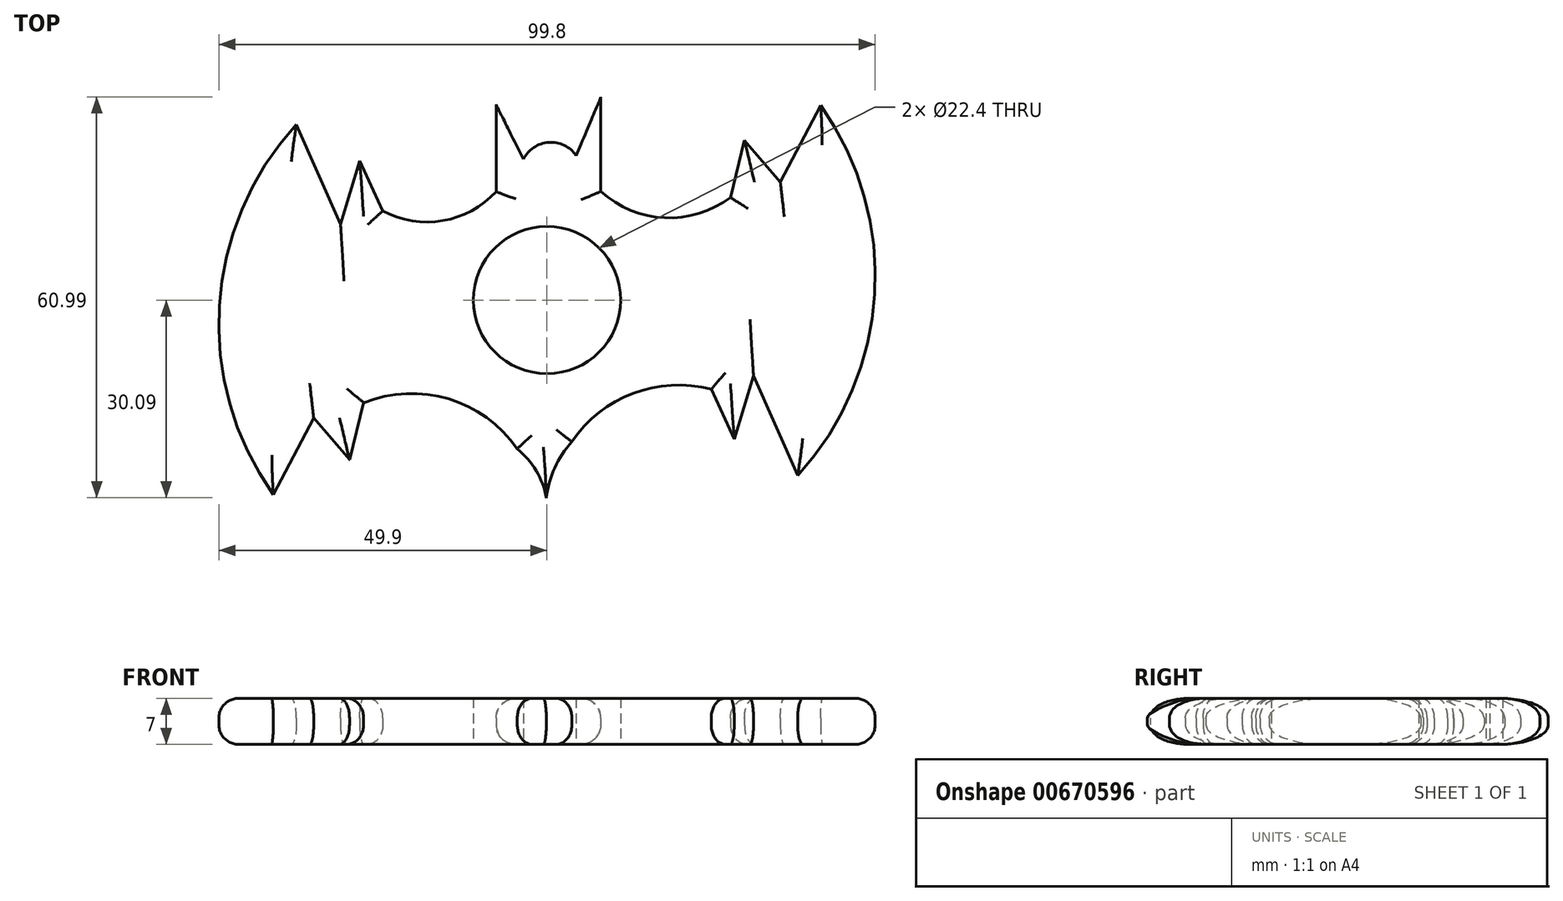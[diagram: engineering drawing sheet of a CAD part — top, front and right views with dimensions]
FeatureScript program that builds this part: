
annotation { "Feature Type Name" : "Feature", "Feature Type Description" : "" }
export const myFeature = defineFeature(function(context is Context, id is Id, definition is map)
    precondition{}
    {
        {
            var Q0;
            Q0=qCreatedBy(makeId("Top.planeOp"),FACE);
            var sketch = newSketch(context, id + "F0", { "sketchPlane" : qUnion([Q0])});
            skCircle(sketch, "E0", {"center": v(0, 0) * mm, "radius": 11.2 * mm});
            skCircle(sketch, "E1", {"center": v(0, 0) * mm, "radius": 13.2 * mm});
            skArc(sketch, "E2", {"start": v(-38.1, 26.72) * mm, "mid": v(-49.82, -0.84) * mm, "end": v(-41.61, -29.64) * mm});
            skArc(sketch, "E3.1.0", {"start": v(38.1, -26.72) * mm, "mid": v(49.82, 0.84) * mm, "end": v(41.61, 29.64) * mm});
            skLineSegment(sketch, "E4", {"start": v(-41.61, -29.64) * mm, "end": v(-35.48, -17.96) * mm});
            skLineSegment(sketch, "E5", {"start": v(-35.48, -17.96) * mm, "end": v(-35.48, -24.97) * mm});
            skArc(sketch, "E6", {"start": v(-4.53, -22.63) * mm, "mid": v(-14.98, -15.03) * mm, "end": v(-27.89, -15.62) * mm});
            skLineSegment(sketch, "E7.1.0", {"start": v(41.61, 29.64) * mm, "end": v(35.48, 17.96) * mm});
            skLineSegment(sketch, "E7.1.1", {"start": v(35.48, 17.96) * mm, "end": v(30.03, 24.29) * mm});
            skLineSegment(sketch, "E7.1.2", {"start": v(30.03, 24.29) * mm, "end": v(27.89, 15.62) * mm});
            skLineSegment(sketch, "E8", {"start": v(38.1, -26.72) * mm, "end": v(31.4, -11.53) * mm});
            skLineSegment(sketch, "E9", {"start": v(31.4, -11.53) * mm, "end": v(28.47, -21.17) * mm});
            skLineSegment(sketch, "E10", {"start": v(28.47, -21.17) * mm, "end": v(24.97, -13.58) * mm});
            skArc(sketch, "E11.1.0", {"start": v(-24.97, 13.58) * mm, "mid": v(-15.85, 12.08) * mm, "end": v(-7.74, 16.5) * mm});
            skLineSegment(sketch, "E11.1.2", {"start": v(-28.47, 21.17) * mm, "end": v(-24.97, 13.58) * mm});
            skLineSegment(sketch, "E11.1.4", {"start": v(-31.4, 11.53) * mm, "end": v(-28.47, 21.17) * mm});
            skLineSegment(sketch, "E11.1.5", {"start": v(-38.1, 26.72) * mm, "end": v(-31.4, 11.53) * mm});
            skArc(sketch, "E12", {"start": v(0, -34.06) * mm, "mid": v(-0.76, -27.75) * mm, "end": v(-4.53, -22.63) * mm});
            skArc(sketch, "E13.1.0", {"start": v(8.2, 16.53) * mm, "mid": v(17.88, 12.52) * mm, "end": v(27.89, 15.62) * mm});
            skLineSegment(sketch, "E14", {"start": v(-7.74, 16.5) * mm, "end": v(-7.74, 29.75) * mm});
            skLineSegment(sketch, "E15", {"start": v(-7.74, 29.75) * mm, "end": v(-3.6, 21.41) * mm});
            skLineSegment(sketch, "E16", {"start": v(8.2, 16.53) * mm, "end": v(8.2, 30.9) * mm});
            skLineSegment(sketch, "E17", {"start": v(8.2, 30.9) * mm, "end": v(4.45, 21.97) * mm});
            skArc(sketch, "E18", {"start": v(4.45, 21.97) * mm, "mid": v(0.27, 24) * mm, "end": v(-3.6, 21.41) * mm});
            skArc(sketch, "E19", {"start": v(24.97, -13.58) * mm, "mid": v(13.1, -14.2) * mm, "end": v(3.78, -21.57) * mm});
            skArc(sketch, "E20", {"start": v(3.78, -21.57) * mm, "mid": v(0.47, -27.38) * mm, "end": v(0, -34.06) * mm});
            skLineSegment(sketch, "E21.1.0", {"start": v(-35.48, -17.96) * mm, "end": v(-30.03, -24.29) * mm});
            skLineSegment(sketch, "E21.1.1", {"start": v(-30.03, -24.29) * mm, "end": v(-27.89, -15.62) * mm});
            skSolve(sketch);
        }
        {
            var Q0;
            Q0=makeQuery(id+"F0.imprint","IMPRINT",FACE,{"disambiguationData":[TD([[makeQuery(id+"F0.imprint","IMPRINT",EDGE,{"derivedFrom":sQuery(id+"F0.wireOp",EDGE,"E0")}),-1.0]])]});
            var Q1;
            Q1=makeQuery(id+"F0.imprint","IMPRINT",FACE,{"disambiguationData":[TD([[makeQuery(id+"F0.imprint","IMPRINT",EDGE,{"derivedFrom":sQuery(id+"F0.wireOp",EDGE,"E1")}),-1.0]])]});
            extrude(context, id + "F1", {"entities" : qUnion([Q0, Q1]), "depth" : 7 * mm, "offsetDistance" : 25 * mm});
        }
        {
            var Q0;
            Q0=makeQuery(id+"F1.opExtrude","CAP_EDGE",EDGE,{"disambiguationData":[OSD([sQuery(id+"F0.wireOp",EDGE,"E20")])],"isStart":false});
            var Q1;
            Q1=makeQuery(id+"F1.opExtrude","CAP_EDGE",EDGE,{"disambiguationData":[OSD([sQuery(id+"F0.wireOp",EDGE,"E19")])],"isStart":false});
            var Q2;
            Q2=makeQuery(id+"F1.opExtrude","CAP_EDGE",EDGE,{"disambiguationData":[OSD([sQuery(id+"F0.wireOp",EDGE,"E9")])],"isStart":false});
            var Q3;
            Q3=makeQuery(id+"F1.opExtrude","CAP_EDGE",EDGE,{"disambiguationData":[OSD([sQuery(id+"F0.wireOp",EDGE,"E3.1.0")])],"isStart":false});
            var Q4;
            Q4=makeQuery(id+"F1.opExtrude","CAP_EDGE",EDGE,{"disambiguationData":[OSD([sQuery(id+"F0.wireOp",EDGE,"E8")])],"isStart":false});
            var Q5;
            Q5=makeQuery(id+"F1.opExtrude","CAP_EDGE",EDGE,{"disambiguationData":[OSD([sQuery(id+"F0.wireOp",EDGE,"E7.1.0")])],"isStart":false});
            var Q6;
            Q6=makeQuery(id+"F1.opExtrude","CAP_EDGE",EDGE,{"disambiguationData":[OSD([sQuery(id+"F0.wireOp",EDGE,"E7.1.1")])],"isStart":false});
            var Q7;
            Q7=makeQuery(id+"F1.opExtrude","CAP_EDGE",EDGE,{"disambiguationData":[OSD([sQuery(id+"F0.wireOp",EDGE,"E7.1.2")])],"isStart":false});
            var Q8;
            Q8=makeQuery(id+"F1.opExtrude","CAP_EDGE",EDGE,{"disambiguationData":[OSD([sQuery(id+"F0.wireOp",EDGE,"E13.1.0")])],"isStart":false});
            var Q9;
            Q9=makeQuery(id+"F1.opExtrude","CAP_EDGE",EDGE,{"disambiguationData":[OSD([sQuery(id+"F0.wireOp",EDGE,"E16")])],"isStart":false});
            var Q10;
            Q10=makeQuery(id+"F1.opExtrude","CAP_EDGE",EDGE,{"disambiguationData":[OSD([sQuery(id+"F0.wireOp",EDGE,"E14")])],"isStart":false});
            var Q11;
            Q11=makeQuery(id+"F1.opExtrude","CAP_EDGE",EDGE,{"disambiguationData":[OSD([sQuery(id+"F0.wireOp",EDGE,"E11.1.0")])],"isStart":false});
            var Q12;
            Q12=makeQuery(id+"F1.opExtrude","CAP_EDGE",EDGE,{"disambiguationData":[OSD([sQuery(id+"F0.wireOp",EDGE,"E11.1.2")])],"isStart":false});
            var Q13;
            Q13=makeQuery(id+"F1.opExtrude","CAP_EDGE",EDGE,{"disambiguationData":[OSD([sQuery(id+"F0.wireOp",EDGE,"E11.1.5")])],"isStart":false});
            var Q14;
            Q14=makeQuery(id+"F1.opExtrude","CAP_EDGE",EDGE,{"disambiguationData":[OSD([sQuery(id+"F0.wireOp",EDGE,"E11.1.4")])],"isStart":false});
            var Q15;
            Q15=makeQuery(id+"F1.opExtrude","CAP_EDGE",EDGE,{"disambiguationData":[OSD([sQuery(id+"F0.wireOp",EDGE,"E2")])],"isStart":false});
            var Q16;
            Q16=makeQuery(id+"F1.opExtrude","CAP_EDGE",EDGE,{"disambiguationData":[OSD([sQuery(id+"F0.wireOp",EDGE,"E4")])],"isStart":false});
            var Q17;
            Q17=makeQuery(id+"F1.opExtrude","CAP_EDGE",EDGE,{"disambiguationData":[OSD([sQuery(id+"F0.wireOp",EDGE,"wEF84jsq-XExs-cQrN-D3yr-Ib7uIkRzdJAm")])],"isStart":false});
            var Q18;
            Q18=makeQuery(id+"F1.opExtrude","CAP_EDGE",EDGE,{"disambiguationData":[OSD([sQuery(id+"F0.wireOp",EDGE,"E12")])],"isStart":false});
            var Q19;
            Q19=makeQuery(id+"F1.opExtrude","CAP_EDGE",EDGE,{"disambiguationData":[OSD([sQuery(id+"F0.wireOp",EDGE,"E5")])],"isStart":false});
            var Q20;
            Q20=makeQuery(id+"F1.opExtrude","CAP_EDGE",EDGE,{"disambiguationData":[OSD([sQuery(id+"F0.wireOp",EDGE,"E10")])],"isStart":false});
            var Q21;
            Q21=makeQuery(id+"F1.opExtrude","CAP_EDGE",EDGE,{"disambiguationData":[OSD([sQuery(id+"F0.wireOp",EDGE,"E21.1.1")])],"isStart":false});
            var Q22;
            Q22=makeQuery(id+"F1.opExtrude","CAP_EDGE",EDGE,{"disambiguationData":[OSD([sQuery(id+"F0.wireOp",EDGE,"E6")])],"isStart":false});
            var Q23;
            Q23=makeQuery(id+"F1.opExtrude","CAP_EDGE",EDGE,{"disambiguationData":[OSD([sQuery(id+"F0.wireOp",EDGE,"E21.1.0")])],"isStart":false});
            var Q24;
            Q24=makeQuery(id+"F1.opExtrude","CAP_EDGE",EDGE,{"disambiguationData":[OSD([sQuery(id+"F0.wireOp",EDGE,"E3.1.0")])],"isStart":true});
            var Q25;
            Q25=makeQuery(id+"F1.opExtrude","CAP_EDGE",EDGE,{"disambiguationData":[OSD([sQuery(id+"F0.wireOp",EDGE,"E8")])],"isStart":true});
            var Q26;
            Q26=makeQuery(id+"F1.opExtrude","CAP_EDGE",EDGE,{"disambiguationData":[OSD([sQuery(id+"F0.wireOp",EDGE,"E9")])],"isStart":true});
            var Q27;
            Q27=makeQuery(id+"F1.opExtrude","CAP_EDGE",EDGE,{"disambiguationData":[OSD([sQuery(id+"F0.wireOp",EDGE,"E10")])],"isStart":true});
            var Q28;
            Q28=makeQuery(id+"F1.opExtrude","CAP_EDGE",EDGE,{"disambiguationData":[OSD([sQuery(id+"F0.wireOp",EDGE,"E19")])],"isStart":true});
            var Q29;
            Q29=makeQuery(id+"F1.opExtrude","CAP_EDGE",EDGE,{"disambiguationData":[OSD([sQuery(id+"F0.wireOp",EDGE,"E6")])],"isStart":true});
            var Q30;
            Q30=makeQuery(id+"F1.opExtrude","CAP_EDGE",EDGE,{"disambiguationData":[OSD([sQuery(id+"F0.wireOp",EDGE,"E12")])],"isStart":true});
            var Q31;
            Q31=makeQuery(id+"F1.opExtrude","CAP_EDGE",EDGE,{"disambiguationData":[OSD([sQuery(id+"F0.wireOp",EDGE,"E20")])],"isStart":true});
            var Q32;
            Q32=makeQuery(id+"F1.opExtrude","CAP_EDGE",EDGE,{"disambiguationData":[OSD([sQuery(id+"F0.wireOp",EDGE,"E21.1.1")])],"isStart":true});
            var Q33;
            Q33=makeQuery(id+"F1.opExtrude","CAP_EDGE",EDGE,{"disambiguationData":[OSD([sQuery(id+"F0.wireOp",EDGE,"E21.1.0")])],"isStart":true});
            var Q34;
            Q34=makeQuery(id+"F1.opExtrude","CAP_EDGE",EDGE,{"disambiguationData":[OSD([sQuery(id+"F0.wireOp",EDGE,"E4")])],"isStart":true});
            var Q35;
            Q35=makeQuery(id+"F1.opExtrude","CAP_EDGE",EDGE,{"disambiguationData":[OSD([sQuery(id+"F0.wireOp",EDGE,"E2")])],"isStart":true});
            var Q36;
            Q36=makeQuery(id+"F1.opExtrude","CAP_EDGE",EDGE,{"disambiguationData":[OSD([sQuery(id+"F0.wireOp",EDGE,"E11.1.5")])],"isStart":true});
            var Q37;
            Q37=makeQuery(id+"F1.opExtrude","CAP_EDGE",EDGE,{"disambiguationData":[OSD([sQuery(id+"F0.wireOp",EDGE,"E11.1.4")])],"isStart":true});
            var Q38;
            Q38=makeQuery(id+"F1.opExtrude","CAP_EDGE",EDGE,{"disambiguationData":[OSD([sQuery(id+"F0.wireOp",EDGE,"E14")])],"isStart":true});
            var Q39;
            Q39=makeQuery(id+"F1.opExtrude","CAP_EDGE",EDGE,{"disambiguationData":[OSD([sQuery(id+"F0.wireOp",EDGE,"E16")])],"isStart":true});
            var Q40;
            Q40=makeQuery(id+"F1.opExtrude","CAP_EDGE",EDGE,{"disambiguationData":[OSD([sQuery(id+"F0.wireOp",EDGE,"E13.1.0")])],"isStart":true});
            var Q41;
            Q41=makeQuery(id+"F1.opExtrude","CAP_EDGE",EDGE,{"disambiguationData":[OSD([sQuery(id+"F0.wireOp",EDGE,"E7.1.2")])],"isStart":true});
            var Q42;
            Q42=makeQuery(id+"F1.opExtrude","CAP_EDGE",EDGE,{"disambiguationData":[OSD([sQuery(id+"F0.wireOp",EDGE,"E7.1.1")])],"isStart":true});
            var Q43;
            Q43=makeQuery(id+"F1.opExtrude","CAP_EDGE",EDGE,{"disambiguationData":[OSD([sQuery(id+"F0.wireOp",EDGE,"E7.1.0")])],"isStart":true});
            var Q44;
            Q44=makeQuery(id+"F1.opExtrude","CAP_EDGE",EDGE,{"disambiguationData":[OSD([sQuery(id+"F0.wireOp",EDGE,"E11.1.0")])],"isStart":true});
            var Q45;
            Q45=makeQuery(id+"F1.opExtrude","CAP_EDGE",EDGE,{"disambiguationData":[OSD([sQuery(id+"F0.wireOp",EDGE,"E11.1.2")])],"isStart":true});
            fillet(context, id + "F2", {"entities" : qUnion([Q0, Q1, Q2, Q3, Q4, Q5, Q6, Q7, Q8, Q9, Q10, Q11, Q12, Q13, Q14, Q15, Q16, Q17, Q18, Q19, Q20, Q21, Q22, Q23, Q24, Q25, Q26, Q27, Q28, Q29, Q30, Q31, Q32, Q33, Q34, Q35, Q36, Q37, Q38, Q39, Q40, Q41, Q42, Q43, Q44, Q45]), "radius" : 3 * mm, "tangentPropagation" : true, "allowEdgeOverflow" : false});
        }
    });
